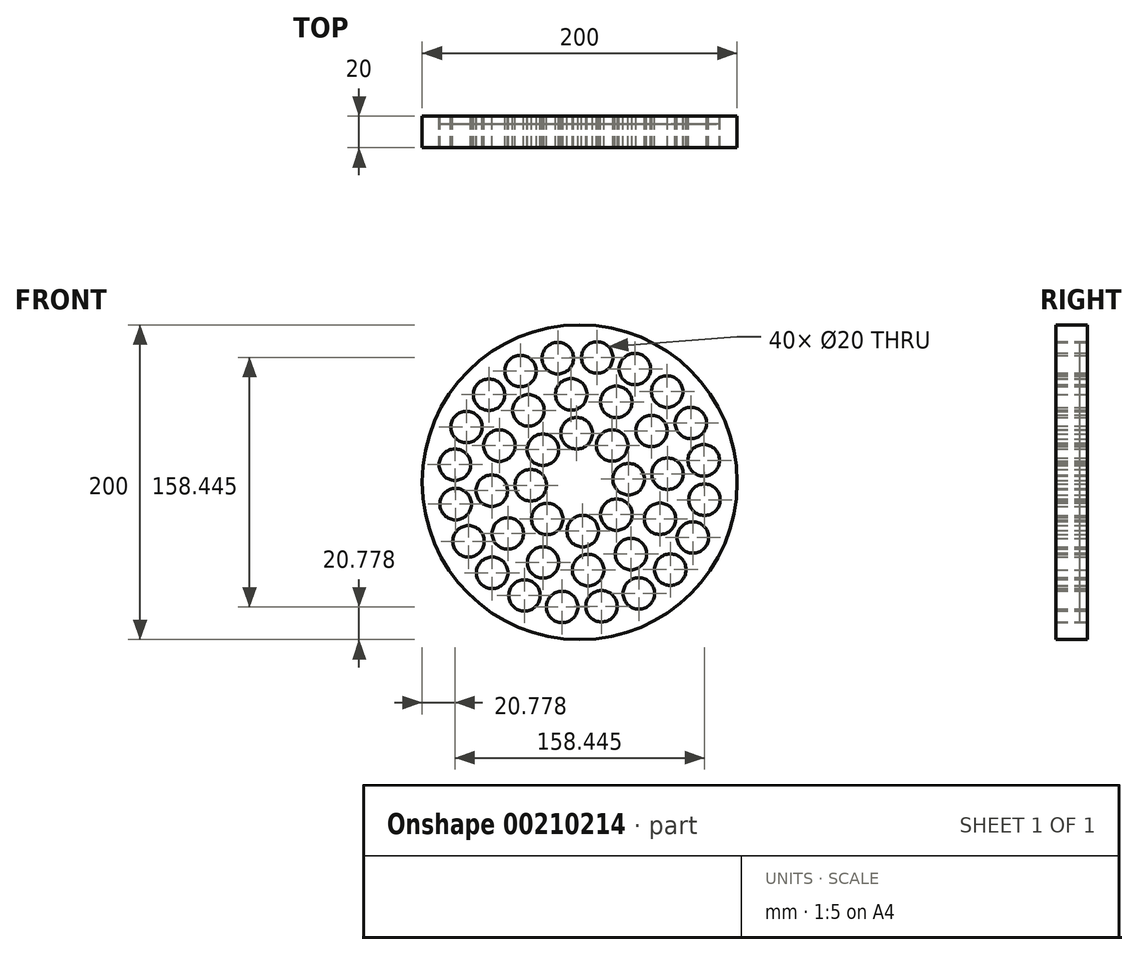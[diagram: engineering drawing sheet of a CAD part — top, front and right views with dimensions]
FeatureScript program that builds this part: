
annotation { "Feature Type Name" : "Feature", "Feature Type Description" : "" }
export const myFeature = defineFeature(function(context is Context, id is Id, definition is map)
    precondition{}
    {
        {
            var Q0;
            Q0=qCreatedBy(makeId("Front.planeOp"),FACE);
            var sketch = newSketch(context, id + "F0", { "sketchPlane" : qUnion([Q0])});
            skCircle(sketch, "E0", {"center": v(0, 0) * mm, "radius": 100 * mm});
            skCircle(sketch, "E1", {"center": v(57.55, -55.57) * mm, "radius": 10 * mm});
            skCircle(sketch, "E2.1.0", {"center": v(71.9, -35.06) * mm, "radius": 10 * mm});
            skCircle(sketch, "E2.2.0", {"center": v(79.22, -11.13) * mm, "radius": 10 * mm});
            skCircle(sketch, "E2.3.0", {"center": v(78.78, 13.9) * mm, "radius": 10 * mm});
            skCircle(sketch, "E2.4.0", {"center": v(70.63, 37.56) * mm, "radius": 10 * mm});
            skCircle(sketch, "E2.5.0", {"center": v(55.57, 57.55) * mm, "radius": 10 * mm});
            skCircle(sketch, "E2.6.0", {"center": v(35.06, 71.9) * mm, "radius": 10 * mm});
            skCircle(sketch, "E2.7.0", {"center": v(11.13, 79.22) * mm, "radius": 10 * mm});
            skCircle(sketch, "E2.8.0", {"center": v(-13.9, 78.78) * mm, "radius": 10 * mm});
            skCircle(sketch, "E2.9.0", {"center": v(-37.56, 70.63) * mm, "radius": 10 * mm});
            skCircle(sketch, "E3.1.10.0", {"center": v(-57.55, 55.57) * mm, "radius": 10 * mm});
            skCircle(sketch, "E3.1.11.0", {"center": v(-71.9, 35.06) * mm, "radius": 10 * mm});
            skCircle(sketch, "E3.1.12.0", {"center": v(-79.22, 11.13) * mm, "radius": 10 * mm});
            skCircle(sketch, "E3.1.13.0", {"center": v(-78.78, -13.9) * mm, "radius": 10 * mm});
            skCircle(sketch, "E3.1.14.0", {"center": v(-70.63, -37.56) * mm, "radius": 10 * mm});
            skCircle(sketch, "E3.1.15.0", {"center": v(-55.57, -57.55) * mm, "radius": 10 * mm});
            skCircle(sketch, "E3.1.16.0", {"center": v(-35.06, -71.9) * mm, "radius": 10 * mm});
            skCircle(sketch, "E3.1.17.0", {"center": v(-11.13, -79.22) * mm, "radius": 10 * mm});
            skCircle(sketch, "E3.1.18.0", {"center": v(13.9, -78.78) * mm, "radius": 10 * mm});
            skCircle(sketch, "E3.1.19.0", {"center": v(37.56, -70.63) * mm, "radius": 10 * mm});
            skCircle(sketch, "E4", {"center": v(-32.55, 45.63) * mm, "radius": 10 * mm});
            skCircle(sketch, "E5.1.0", {"center": v(-51, 23.24) * mm, "radius": 10 * mm});
            skCircle(sketch, "E5.2.0", {"center": v(-55.8, -5.37) * mm, "radius": 10 * mm});
            skCircle(sketch, "E5.3.0", {"center": v(-45.63, -32.55) * mm, "radius": 10 * mm});
            skCircle(sketch, "E5.4.0", {"center": v(-23.24, -51) * mm, "radius": 10 * mm});
            skCircle(sketch, "E5.5.0", {"center": v(5.37, -55.8) * mm, "radius": 10 * mm});
            skCircle(sketch, "E5.6.0", {"center": v(32.55, -45.63) * mm, "radius": 10 * mm});
            skCircle(sketch, "E5.7.0", {"center": v(51, -23.24) * mm, "radius": 10 * mm});
            skCircle(sketch, "E5.8.0", {"center": v(55.8, 5.37) * mm, "radius": 10 * mm});
            skCircle(sketch, "E5.9.0", {"center": v(45.63, 32.55) * mm, "radius": 10 * mm});
            skCircle(sketch, "E5.10.0", {"center": v(23.24, 51) * mm, "radius": 10 * mm});
            skCircle(sketch, "E5.11.0", {"center": v(-5.37, 55.8) * mm, "radius": 10 * mm});
            skCircle(sketch, "E6", {"center": v(-20.63, -23.34) * mm, "radius": 10 * mm});
            skCircle(sketch, "E7.1.0", {"center": v(1.92, -31.09) * mm, "radius": 10 * mm});
            skCircle(sketch, "E7.2.0", {"center": v(23.34, -20.63) * mm, "radius": 10 * mm});
            skCircle(sketch, "E7.3.0", {"center": v(31.09, 1.92) * mm, "radius": 10 * mm});
            skCircle(sketch, "E7.4.0", {"center": v(20.63, 23.34) * mm, "radius": 10 * mm});
            skCircle(sketch, "E7.5.0", {"center": v(-1.92, 31.09) * mm, "radius": 10 * mm});
            skCircle(sketch, "E7.6.0", {"center": v(-23.34, 20.63) * mm, "radius": 10 * mm});
            skCircle(sketch, "E7.7.0", {"center": v(-31.09, -1.92) * mm, "radius": 10 * mm});
            skSolve(sketch);
        }
        {
            var Q0;
            Q0=makeQuery(id+"F0.imprint","IMPRINT",FACE,{"disambiguationData":[TD([[makeQuery(id+"F0.imprint","IMPRINT",EDGE,{"derivedFrom":sQuery(id+"F0.wireOp",EDGE,"E3.1.10.0")}),1.0]])]});
            var Q1;
            Q1=makeQuery(id+"F0.imprint","IMPRINT",FACE,{"disambiguationData":[TD([[makeQuery(id+"F0.imprint","IMPRINT",EDGE,{"derivedFrom":sQuery(id+"F0.wireOp",EDGE,"E7.5.0")}),1.0]])]});
            var Q2;
            Q2=makeQuery(id+"F0.imprint","IMPRINT",FACE,{"disambiguationData":[TD([[makeQuery(id+"F0.imprint","IMPRINT",EDGE,{"derivedFrom":sQuery(id+"F0.wireOp",EDGE,"E2.8.0")}),1.0]])]});
            var Q3;
            Q3=makeQuery(id+"F0.imprint","IMPRINT",FACE,{"disambiguationData":[TD([[makeQuery(id+"F0.imprint","IMPRINT",EDGE,{"derivedFrom":sQuery(id+"F0.wireOp",EDGE,"E5.10.0")}),1.0]])]});
            var Q4;
            Q4=makeQuery(id+"F0.imprint","IMPRINT",FACE,{"disambiguationData":[TD([[makeQuery(id+"F0.imprint","IMPRINT",EDGE,{"derivedFrom":sQuery(id+"F0.wireOp",EDGE,"E5.8.0")}),1.0]])]});
            var Q5;
            Q5=makeQuery(id+"F0.imprint","IMPRINT",FACE,{"disambiguationData":[TD([[makeQuery(id+"F0.imprint","IMPRINT",EDGE,{"derivedFrom":sQuery(id+"F0.wireOp",EDGE,"E7.1.0")}),1.0]])]});
            var Q6;
            Q6=makeQuery(id+"F0.imprint","IMPRINT",FACE,{"disambiguationData":[TD([[makeQuery(id+"F0.imprint","IMPRINT",EDGE,{"derivedFrom":sQuery(id+"F0.wireOp",EDGE,"E2.5.0")}),1.0]])]});
            var Q7;
            Q7=makeQuery(id+"F0.imprint","IMPRINT",FACE,{"disambiguationData":[TD([[makeQuery(id+"F0.imprint","IMPRINT",EDGE,{"derivedFrom":sQuery(id+"F0.wireOp",EDGE,"E2.7.0")}),1.0]])]});
            var Q8;
            Q8=makeQuery(id+"F0.imprint","IMPRINT",FACE,{"disambiguationData":[TD([[makeQuery(id+"F0.imprint","IMPRINT",EDGE,{"derivedFrom":sQuery(id+"F0.wireOp",EDGE,"E7.6.0")}),1.0]])]});
            var Q9;
            Q9=makeQuery(id+"F0.imprint","IMPRINT",FACE,{"disambiguationData":[TD([[makeQuery(id+"F0.imprint","IMPRINT",EDGE,{"derivedFrom":sQuery(id+"F0.wireOp",EDGE,"E5.7.0")}),1.0]])]});
            var Q10;
            Q10=makeQuery(id+"F0.imprint","IMPRINT",FACE,{"disambiguationData":[TD([[makeQuery(id+"F0.imprint","IMPRINT",EDGE,{"derivedFrom":sQuery(id+"F0.wireOp",EDGE,"E5.2.0")}),1.0]])]});
            var Q11;
            Q11=makeQuery(id+"F0.imprint","IMPRINT",FACE,{"disambiguationData":[TD([[makeQuery(id+"F0.imprint","IMPRINT",EDGE,{"derivedFrom":sQuery(id+"F0.wireOp",EDGE,"E7.7.0")}),1.0]])]});
            var Q12;
            Q12=makeQuery(id+"F0.imprint","IMPRINT",FACE,{"disambiguationData":[TD([[makeQuery(id+"F0.imprint","IMPRINT",EDGE,{"derivedFrom":sQuery(id+"F0.wireOp",EDGE,"E5.1.0")}),1.0]])]});
            var Q13;
            Q13=makeQuery(id+"F0.imprint","IMPRINT",FACE,{"disambiguationData":[TD([[makeQuery(id+"F0.imprint","IMPRINT",EDGE,{"derivedFrom":sQuery(id+"F0.wireOp",EDGE,"E3.1.13.0")}),1.0]])]});
            var Q14;
            Q14=makeQuery(id+"F0.imprint","IMPRINT",FACE,{"disambiguationData":[TD([[makeQuery(id+"F0.imprint","IMPRINT",EDGE,{"derivedFrom":sQuery(id+"F0.wireOp",EDGE,"E7.4.0")}),1.0]])]});
            var Q15;
            Q15=makeQuery(id+"F0.imprint","IMPRINT",FACE,{"disambiguationData":[TD([[makeQuery(id+"F0.imprint","IMPRINT",EDGE,{"derivedFrom":sQuery(id+"F0.wireOp",EDGE,"E3.1.12.0")}),1.0]])]});
            var Q16;
            Q16=makeQuery(id+"F0.imprint","IMPRINT",FACE,{"disambiguationData":[TD([[makeQuery(id+"F0.imprint","IMPRINT",EDGE,{"derivedFrom":sQuery(id+"F0.wireOp",EDGE,"E3.1.19.0")}),1.0]])]});
            var Q17;
            Q17=makeQuery(id+"F0.imprint","IMPRINT",FACE,{"disambiguationData":[TD([[makeQuery(id+"F0.imprint","IMPRINT",EDGE,{"derivedFrom":sQuery(id+"F0.wireOp",EDGE,"E4")}),1.0]])]});
            var Q18;
            Q18=makeQuery(id+"F0.imprint","IMPRINT",FACE,{"disambiguationData":[TD([[makeQuery(id+"F0.imprint","IMPRINT",EDGE,{"derivedFrom":sQuery(id+"F0.wireOp",EDGE,"E5.6.0")}),1.0]])]});
            var Q19;
            Q19=makeQuery(id+"F0.imprint","IMPRINT",FACE,{"disambiguationData":[TD([[makeQuery(id+"F0.imprint","IMPRINT",EDGE,{"derivedFrom":sQuery(id+"F0.wireOp",EDGE,"E5.11.0")}),1.0]])]});
            var Q20;
            Q20=makeQuery(id+"F0.imprint","IMPRINT",FACE,{"disambiguationData":[TD([[makeQuery(id+"F0.imprint","IMPRINT",EDGE,{"derivedFrom":sQuery(id+"F0.wireOp",EDGE,"E5.4.0")}),1.0]])]});
            var Q21;
            Q21=makeQuery(id+"F0.imprint","IMPRINT",FACE,{"disambiguationData":[TD([[makeQuery(id+"F0.imprint","IMPRINT",EDGE,{"derivedFrom":sQuery(id+"F0.wireOp",EDGE,"E5.5.0")}),1.0]])]});
            var Q22;
            Q22=makeQuery(id+"F0.imprint","IMPRINT",FACE,{"disambiguationData":[TD([[makeQuery(id+"F0.imprint","IMPRINT",EDGE,{"derivedFrom":sQuery(id+"F0.wireOp",EDGE,"E2.4.0")}),1.0]])]});
            var Q23;
            Q23=makeQuery(id+"F0.imprint","IMPRINT",FACE,{"disambiguationData":[TD([[makeQuery(id+"F0.imprint","IMPRINT",EDGE,{"derivedFrom":sQuery(id+"F0.wireOp",EDGE,"E3.1.18.0")}),1.0]])]});
            var Q24;
            Q24=makeQuery(id+"F0.imprint","IMPRINT",FACE,{"disambiguationData":[TD([[makeQuery(id+"F0.imprint","IMPRINT",EDGE,{"derivedFrom":sQuery(id+"F0.wireOp",EDGE,"E3.1.16.0")}),1.0]])]});
            var Q25;
            Q25=makeQuery(id+"F0.imprint","IMPRINT",FACE,{"disambiguationData":[TD([[makeQuery(id+"F0.imprint","IMPRINT",EDGE,{"derivedFrom":sQuery(id+"F0.wireOp",EDGE,"E2.3.0")}),1.0]])]});
            var Q26;
            Q26=makeQuery(id+"F0.imprint","IMPRINT",FACE,{"disambiguationData":[TD([[makeQuery(id+"F0.imprint","IMPRINT",EDGE,{"derivedFrom":sQuery(id+"F0.wireOp",EDGE,"E1")}),1.0]])]});
            var Q27;
            Q27=makeQuery(id+"F0.imprint","IMPRINT",FACE,{"disambiguationData":[TD([[makeQuery(id+"F0.imprint","IMPRINT",EDGE,{"derivedFrom":sQuery(id+"F0.wireOp",EDGE,"E5.3.0")}),1.0]])]});
            var Q28;
            Q28=makeQuery(id+"F0.imprint","IMPRINT",FACE,{"disambiguationData":[TD([[makeQuery(id+"F0.imprint","IMPRINT",EDGE,{"derivedFrom":sQuery(id+"F0.wireOp",EDGE,"E2.2.0")}),1.0]])]});
            var Q29;
            Q29=makeQuery(id+"F0.imprint","IMPRINT",FACE,{"disambiguationData":[TD([[makeQuery(id+"F0.imprint","IMPRINT",EDGE,{"derivedFrom":sQuery(id+"F0.wireOp",EDGE,"E6")}),1.0]])]});
            var Q30;
            Q30=makeQuery(id+"F0.imprint","IMPRINT",FACE,{"disambiguationData":[TD([[makeQuery(id+"F0.imprint","IMPRINT",EDGE,{"derivedFrom":sQuery(id+"F0.wireOp",EDGE,"E2.9.0")}),1.0]])]});
            var Q31;
            Q31=makeQuery(id+"F0.imprint","IMPRINT",FACE,{"disambiguationData":[TD([[makeQuery(id+"F0.imprint","IMPRINT",EDGE,{"derivedFrom":sQuery(id+"F0.wireOp",EDGE,"E2.1.0")}),1.0]])]});
            var Q32;
            Q32=makeQuery(id+"F0.imprint","IMPRINT",FACE,{"disambiguationData":[TD([[makeQuery(id+"F0.imprint","IMPRINT",EDGE,{"derivedFrom":sQuery(id+"F0.wireOp",EDGE,"E3.1.17.0")}),1.0]])]});
            var Q33;
            Q33=makeQuery(id+"F0.imprint","IMPRINT",FACE,{"disambiguationData":[TD([[makeQuery(id+"F0.imprint","IMPRINT",EDGE,{"derivedFrom":sQuery(id+"F0.wireOp",EDGE,"E2.6.0")}),1.0]])]});
            var Q34;
            Q34=makeQuery(id+"F0.imprint","IMPRINT",FACE,{"disambiguationData":[TD([[makeQuery(id+"F0.imprint","IMPRINT",EDGE,{"derivedFrom":sQuery(id+"F0.wireOp",EDGE,"E3.1.14.0")}),1.0]])]});
            var Q35;
            Q35=makeQuery(id+"F0.imprint","IMPRINT",FACE,{"disambiguationData":[TD([[makeQuery(id+"F0.imprint","IMPRINT",EDGE,{"derivedFrom":sQuery(id+"F0.wireOp",EDGE,"E7.3.0")}),1.0]])]});
            var Q36;
            Q36=makeQuery(id+"F0.imprint","IMPRINT",FACE,{"disambiguationData":[TD([[makeQuery(id+"F0.imprint","IMPRINT",EDGE,{"derivedFrom":sQuery(id+"F0.wireOp",EDGE,"E5.9.0")}),1.0]])]});
            var Q37;
            Q37=makeQuery(id+"F0.imprint","IMPRINT",FACE,{"disambiguationData":[TD([[makeQuery(id+"F0.imprint","IMPRINT",EDGE,{"derivedFrom":sQuery(id+"F0.wireOp",EDGE,"E7.2.0")}),1.0]])]});
            var Q38;
            Q38=makeQuery(id+"F0.imprint","IMPRINT",FACE,{"disambiguationData":[TD([[makeQuery(id+"F0.imprint","IMPRINT",EDGE,{"derivedFrom":sQuery(id+"F0.wireOp",EDGE,"E3.1.15.0")}),1.0]])]});
            var Q39;
            Q39=makeQuery(id+"F0.imprint","IMPRINT",FACE,{"disambiguationData":[TD([[makeQuery(id+"F0.imprint","IMPRINT",EDGE,{"derivedFrom":sQuery(id+"F0.wireOp",EDGE,"E3.1.11.0")}),1.0]])]});
            extrude(context, id + "F1", {"entities" : qUnion([Q0, Q1, Q2, Q3, Q4, Q5, Q6, Q7, Q8, Q9, Q10, Q11, Q12, Q13, Q14, Q15, Q16, Q17, Q18, Q19, Q20, Q21, Q22, Q23, Q24, Q25, Q26, Q27, Q28, Q29, Q30, Q31, Q32, Q33, Q34, Q35, Q36, Q37, Q38, Q39]), "depth" : 5 * mm});
        }
        {
            var Q0;
            Q0 = qSketchRegion(id + "F0", true);
            extrude(context, id + "F2", {"entities" : qUnion([Q0]), "depth" : 20 * mm});
        }
    });
